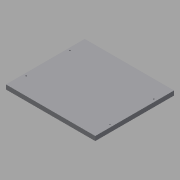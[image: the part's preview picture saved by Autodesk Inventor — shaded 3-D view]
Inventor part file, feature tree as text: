
AUTODESK INVENTOR PART (.ipt)
format: ipt  version: 2014 (Build 180170000, 170)  size: 118,784 bytes
history: native  units: mm
features: extrude x2, sketch x2, projected_geometry x1
ambient origin geometry x8: Origin, YZ Plane, XZ Plane, XY Plane, X Axis, Y Axis, Z Axis, Center Point
bodies: Solid1 (feature_tree)
feature tree (5):
  extrude  "Extrusion1"  Depth=450.0mm
  extrude  "Extrusion2"  Depth=11.0mm
  sketch  "Sketch1"  dims[d0=510.0mm d1=450.0mm]
  sketch  "Sketch2"  dims[d2=25.0mm d3=0.0mm d4=100.0mm d5=100.0mm d6=239.5mm d7=239.5mm d8=7.0mm d9=7.0mm d10=239.5mm d11=239.5mm d12=7.0mm d13=7.0mm d14=11.0mm d15=0.0mm]
  projected_geometry  "Projected Loop1"
